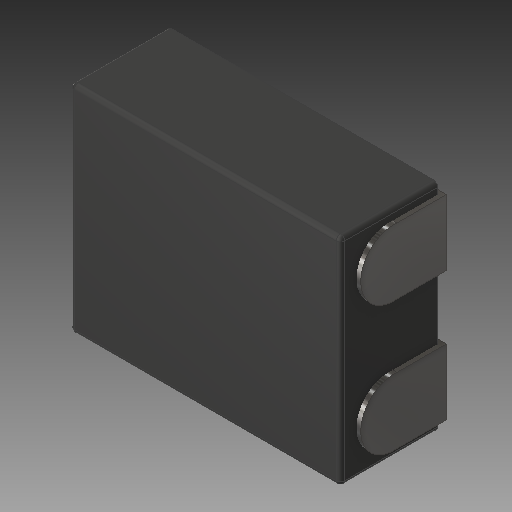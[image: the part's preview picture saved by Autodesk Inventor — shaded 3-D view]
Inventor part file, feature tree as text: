
AUTODESK INVENTOR PART (.ipt)
format: ipt  version: 2019 (Build 230136000, 136)  size: 155,648 bytes
history: native  units: mm
features: other x6, plane x3, extrude x2, sketch x2, mirror x1, fillet x1
ambient origin geometry x8: Origin, YZ Plane, XZ Plane, XY Plane, X Axis, Y Axis, Z Axis, Center Point
bodies: Body1 (feature_tree), Body2 (feature_tree), Body3 (feature_tree)
feature tree (15):
  other  "Sólido1"
  extrude  "Extrusión1"  Depth=1.0mm
  plane  "Plano de trabajo1"
  extrude  "Extrusión2"  TaperAngle=90.0deg  [1 undecoded]
  other  "Edición directa1"
  plane  "Plano de trabajo3"
  mirror  "Simetría1"
  fillet  "Empalme1"  Radius=0.3mm
  sketch  "Boceto1"  dims[d0=1.25mm d1=1.0mm]
  sketch  "Boceto2"  dims[d2=0.45mm d3=0.0mm d4=90.0deg d5=0.3mm d6=0.0mm d7=0.0mm d8=-0.02mm d9=-0.02mm d10=90.0deg d11=0.02mm]
  other  "Sólido2"
  plane  "Plano de trabajo2"
  other  "Patrón de Sólido2:1"
  other  "Sólido3"
  other  "Desplazar1"
note: 1 required parameter value undecoded (feature->parameter linkage not recoverable at this tier; creation-order binding heuristic only, values carry confidence <= 0.55)
